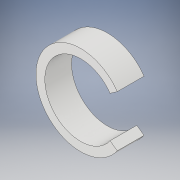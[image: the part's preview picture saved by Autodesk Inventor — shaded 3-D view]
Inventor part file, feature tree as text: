
AUTODESK INVENTOR PART (.ipt)
format: ipt  version: 2017 (Build 210142000, 142)  size: 113,152 bytes
history: native  units: in
note: dims shown in document units (in); Inventor stores cm internally (conversion verified against a paired STEP export)
features: extrude x2, sketch x2
ambient origin geometry x8: Origin, YZ Plane, XZ Plane, XY Plane, X Axis, Y Axis, Z Axis, Center Point
bodies: Solid1 (feature_tree)
feature tree (4):
  extrude  "Extrusion1"  Depth=1.0551in
  extrude  "Extrusion5"  Depth=0.3937in
  sketch  "Sketch1"  dims[d0=1.316in d1=1.0551in]
  sketch  "Sketch5"  dims[d2=0.3937in d3=0.0in d27=0.2405in d28=0.2405in d29=0.3937in d30=0.0in]
